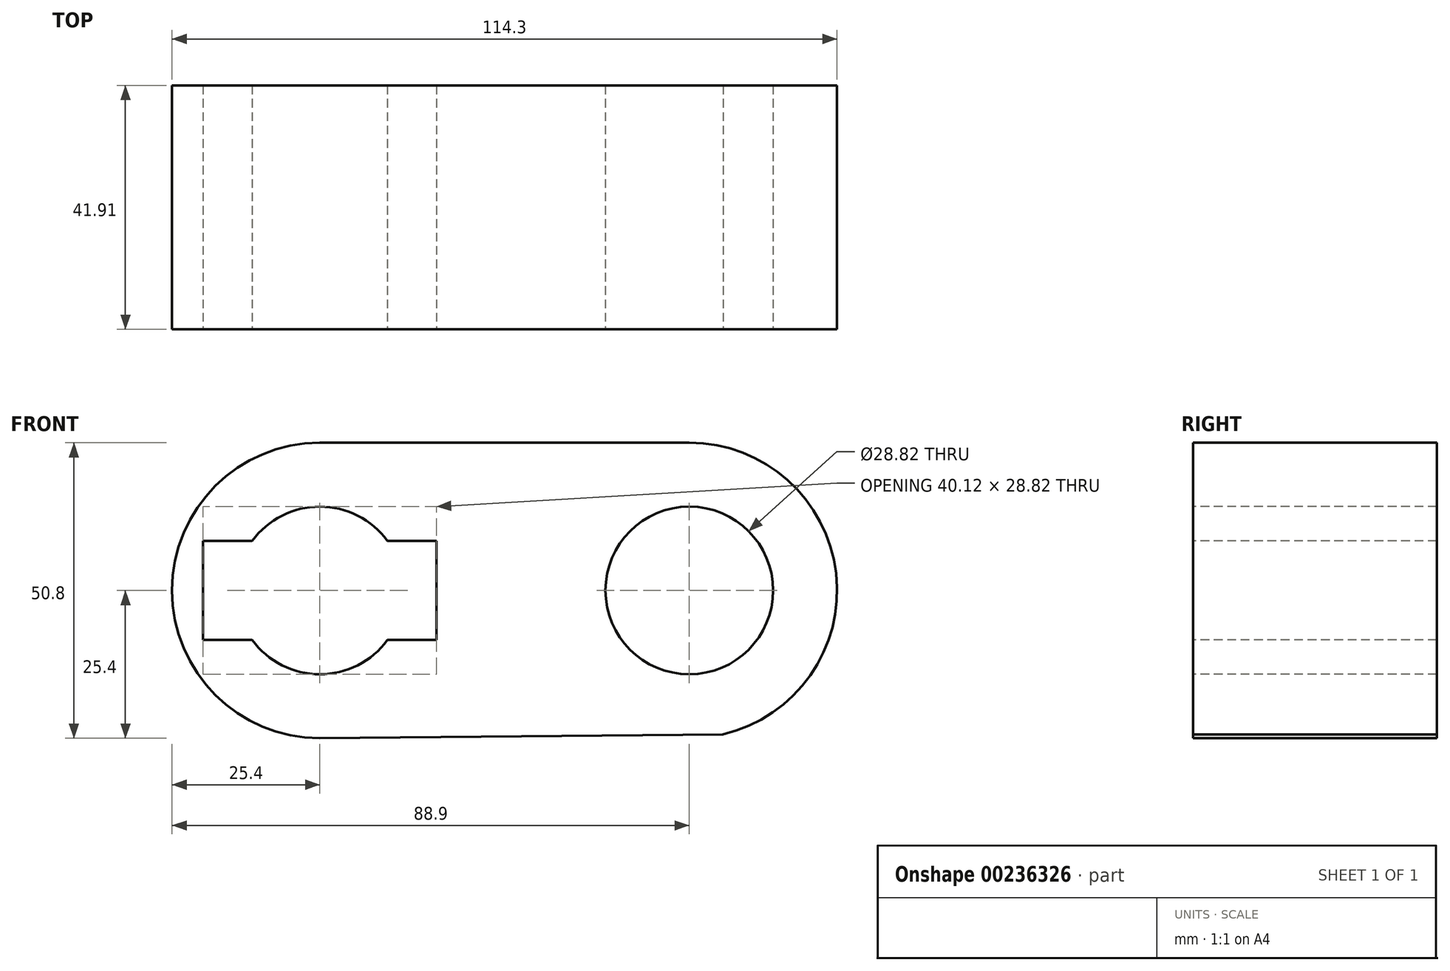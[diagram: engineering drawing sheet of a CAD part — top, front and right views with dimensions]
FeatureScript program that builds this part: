
annotation { "Feature Type Name" : "Feature", "Feature Type Description" : "" }
export const myFeature = defineFeature(function(context is Context, id is Id, definition is map)
    precondition{}
    {
        {
            var Q0;
            Q0=qCreatedBy(makeId("Front.planeOp"),FACE);
            var sketch = newSketch(context, id + "F0", { "sketchPlane" : qUnion([Q0])});
            skCircle(sketch, "E0", {"center": v(0, 0) * mm, "radius": 25.4 * mm});
            skPoint(sketch, "E1.center.orphan", {"position": v(63.5, 0) * mm});
            skCircle(sketch, "E2", {"center": v(63.5, 0) * mm, "radius": 25.4 * mm});
            skLineSegment(sketch, "E3", {"start": v(0, -25.4) * mm, "end": v(69.3, -24.73) * mm});
            skLineSegment(sketch, "E4", {"start": v(0, 25.4) * mm, "end": v(69.3, 25.4) * mm});
            skCircle(sketch, "E5", {"center": v(0, 0) * mm, "radius": 14.41 * mm});
            skCircle(sketch, "E6", {"center": v(63.5, 0) * mm, "radius": 14.41 * mm});
            skLineSegment(sketch, "E7.bottom", {"start": v(20.06, 8.52) * mm, "end": v(-20.06, 8.52) * mm});
            skLineSegment(sketch, "E7.top", {"start": v(20.06, -8.52) * mm, "end": v(-20.06, -8.52) * mm});
            skLineSegment(sketch, "E7.left", {"start": v(20.06, 8.52) * mm, "end": v(20.06, -8.52) * mm});
            skLineSegment(sketch, "E7.right", {"start": v(-20.06, 8.52) * mm, "end": v(-20.06, -8.52) * mm});
            skSolve(sketch);
        }
        {
            var Q0;
            {var subQ0=sQuery(id+"F0.wireOp",EDGE,"E7.left");Q0=makeQuery(id+"F0.imprint","IMPRINT",FACE,{"disambiguationData":[TD([[makeQuery(id+"F0.imprint","IMPRINT",EDGE,{"derivedFrom":subQ0}),1.0]])]});}
            var Q1;
            {var subQ0=sQuery(id+"F0.wireOp",EDGE,"E4");var subQ1=sQuery(id+"F0.wireOp",EDGE,"E0");var subQ2=makeQuery(id+"F0.imprint","INTERSECT",VERTEX,{"derivedFrom":[subQ1,subQ0]});Q1=makeQuery(id+"F0.imprint","IMPRINT",FACE,{"disambiguationData":[TD([[makeQuery(id+"F0.imprint","IMPRINT",EDGE,{"disambiguationData":[TD([[subQ2,1.0]])],"derivedFrom":subQ1}),-1.0]])]});}
            var Q2;
            Q2=makeQuery(id+"F0.imprint","IMPRINT",FACE,{"disambiguationData":[TD([[makeQuery(id+"F0.imprint","IMPRINT",EDGE,{"derivedFrom":sQuery(id+"F0.wireOp",EDGE,"E6")}),-1.0]])]});
            var Q3;
            Q3=makeQuery(id+"F0.imprint","IMPRINT",FACE,{"disambiguationData":[TD([[makeQuery(id+"F0.imprint","IMPRINT",EDGE,{"derivedFrom":sQuery(id+"F0.wireOp",EDGE,"E6")}),1.0]])]});
            var Q4;
            {var subQ5=sQuery(id+"F0.wireOp",EDGE,"E7.right");Q4=makeQuery(id+"F0.imprint","IMPRINT",FACE,{"disambiguationData":[TD([[makeQuery(id+"F0.imprint","IMPRINT",EDGE,{"derivedFrom":subQ5}),1.0]])]});}
            var Q5;
            {var subQ0=sQuery(id+"F0.wireOp",EDGE,"E7.bottom");var subQ1=sQuery(id+"F0.wireOp",EDGE,"E5");var subQ2=makeQuery(id+"F0.imprint","INTERSECT",VERTEX,{"disambiguationData":[OD(0.0)],"derivedFrom":[subQ1,subQ0]});Q5=makeQuery(id+"F0.imprint","IMPRINT",FACE,{"disambiguationData":[TD([[makeQuery(id+"F0.imprint","IMPRINT",EDGE,{"disambiguationData":[TD([[subQ2,1.0]])],"derivedFrom":subQ1}),1.0]])]});}
            var Q6;
            {var subQ0=sQuery(id+"F0.wireOp",EDGE,"E7.bottom");var subQ1=sQuery(id+"F0.wireOp",EDGE,"E5");var subQ2=makeQuery(id+"F0.imprint","INTERSECT",VERTEX,{"disambiguationData":[OD(0.0)],"derivedFrom":[subQ1,subQ0]});Q6=makeQuery(id+"F0.imprint","IMPRINT",FACE,{"disambiguationData":[TD([[makeQuery(id+"F0.imprint","IMPRINT",EDGE,{"disambiguationData":[TD([[subQ2,-1.0]])],"derivedFrom":subQ1}),1.0]])]});}
            var Q7;
            {var subQ0=sQuery(id+"F0.wireOp",EDGE,"E7.top");var subQ1=sQuery(id+"F0.wireOp",EDGE,"E5");var subQ2=makeQuery(id+"F0.imprint","INTERSECT",VERTEX,{"disambiguationData":[OD(0.0)],"derivedFrom":[subQ1,subQ0]});Q7=makeQuery(id+"F0.imprint","IMPRINT",FACE,{"disambiguationData":[TD([[makeQuery(id+"F0.imprint","IMPRINT",EDGE,{"disambiguationData":[TD([[subQ2,-1.0]])],"derivedFrom":subQ1}),1.0]])]});}
            var Q8;
            {var subQ5=sQuery(id+"F0.wireOp",EDGE,"E7.left");Q8=makeQuery(id+"F0.imprint","IMPRINT",FACE,{"disambiguationData":[TD([[makeQuery(id+"F0.imprint","IMPRINT",EDGE,{"derivedFrom":subQ5}),-1.0]])]});}
            extrude(context, id + "F1", {"entities" : qUnion([Q0, Q1, Q2, Q3, Q4, Q5, Q6, Q7, Q8]), "oppositeDirection" : true, "depth" : 41.9 * mm});
        }
        {
            var Q0;
            Q0=makeQuery(id+"F1.opExtrude","SWEPT_FACE",FACE,{"disambiguationData":[OSD([sQuery(id+"F0.wireOp",EDGE,"E4")])]});
            var sketch = newSketch(context, id + "F2", { "sketchPlane" : qUnion([Q0])});
            skText(sketch, "E8", { "text": "ALLISON\n", "fontName": "NotoSansCJKjp-Bold.otf"});
            const initialGuessF2  = {"E8": [0.00406, 0.0134, 1, 0, 0.009]};
            skSetInitialGuess(sketch, initialGuessF2);
            skSolve(sketch);
        }
        {
            var Q0;
            Q0 = qSketchRegion(id + "F2", true);
            extrude(context, id + "F3", {"entities" : qUnion([Q0]), "operationType" : NewBodyOperationType.ADD, "oppositeDirection" : true, "depth" : 14.73 * mm});
        }
        {
            var Q0;
            {var subQ5=sQuery(id+"F0.wireOp",EDGE,"E7.right");Q0=makeQuery(id+"F0.imprint","IMPRINT",FACE,{"disambiguationData":[TD([[makeQuery(id+"F0.imprint","IMPRINT",EDGE,{"derivedFrom":subQ5}),1.0]])]});}
            var Q1;
            {var subQ0=sQuery(id+"F0.wireOp",EDGE,"E7.bottom");var subQ1=sQuery(id+"F0.wireOp",EDGE,"E5");var subQ2=makeQuery(id+"F0.imprint","INTERSECT",VERTEX,{"disambiguationData":[OD(0.0)],"derivedFrom":[subQ1,subQ0]});Q1=makeQuery(id+"F0.imprint","IMPRINT",FACE,{"disambiguationData":[TD([[makeQuery(id+"F0.imprint","IMPRINT",EDGE,{"disambiguationData":[TD([[subQ2,-1.0]])],"derivedFrom":subQ1}),1.0]])]});}
            var Q2;
            {var subQ5=sQuery(id+"F0.wireOp",EDGE,"E7.left");Q2=makeQuery(id+"F0.imprint","IMPRINT",FACE,{"disambiguationData":[TD([[makeQuery(id+"F0.imprint","IMPRINT",EDGE,{"derivedFrom":subQ5}),-1.0]])]});}
            var Q3;
            {var subQ0=sQuery(id+"F0.wireOp",EDGE,"E7.bottom");var subQ1=sQuery(id+"F0.wireOp",EDGE,"E5");var subQ2=makeQuery(id+"F0.imprint","INTERSECT",VERTEX,{"disambiguationData":[OD(0.0)],"derivedFrom":[subQ1,subQ0]});Q3=makeQuery(id+"F0.imprint","IMPRINT",FACE,{"disambiguationData":[TD([[makeQuery(id+"F0.imprint","IMPRINT",EDGE,{"disambiguationData":[TD([[subQ2,1.0]])],"derivedFrom":subQ1}),1.0]])]});}
            var Q4;
            {var subQ0=sQuery(id+"F0.wireOp",EDGE,"E7.top");var subQ1=sQuery(id+"F0.wireOp",EDGE,"E5");var subQ2=makeQuery(id+"F0.imprint","INTERSECT",VERTEX,{"disambiguationData":[OD(0.0)],"derivedFrom":[subQ1,subQ0]});Q4=makeQuery(id+"F0.imprint","IMPRINT",FACE,{"disambiguationData":[TD([[makeQuery(id+"F0.imprint","IMPRINT",EDGE,{"disambiguationData":[TD([[subQ2,-1.0]])],"derivedFrom":subQ1}),1.0]])]});}
            var Q5;
            Q5=makeQuery(id+"F0.imprint","IMPRINT",FACE,{"disambiguationData":[TD([[makeQuery(id+"F0.imprint","IMPRINT",EDGE,{"derivedFrom":sQuery(id+"F0.wireOp",EDGE,"E6")}),1.0]])]});
            extrude(context, id + "F4", {"entities" : qUnion([Q0, Q1, Q2, Q3, Q4, Q5]), "operationType" : NewBodyOperationType.REMOVE, "oppositeDirection" : true, "depth" : 119.38 * mm});
        }
    });
